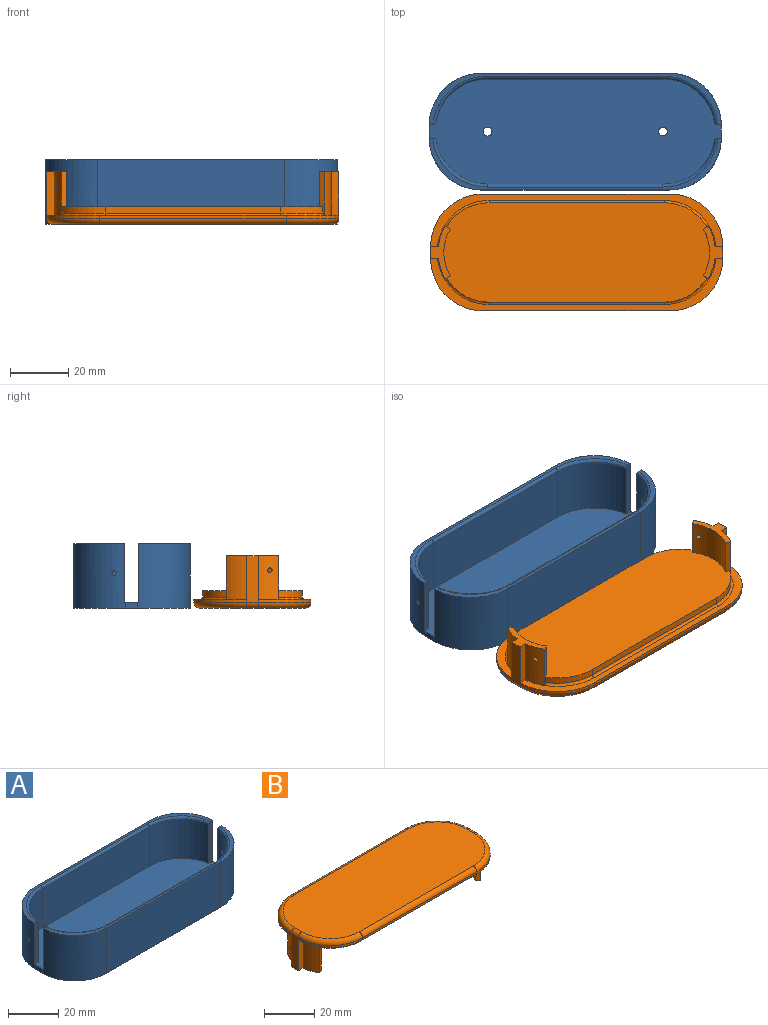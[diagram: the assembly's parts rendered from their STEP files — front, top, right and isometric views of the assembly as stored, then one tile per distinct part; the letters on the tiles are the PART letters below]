
ASSEMBLY  parts=2 mates=1
PART A: 32 faces, bbox 102.3x42.7x22 mm
  f0: plane 4x2mm, normal (1,0,0), area 8mm2, adj f3,f4,f13,f17
  f1: plane 99.99x17.5mm, normal (0,0,1), area 148.6mm2, adj f4,f5,f8,f11,f20,f21,f24,f27
  f2: cylinder r=18mm len=19mm, axis (0,0,-1), area 489.6mm2, adj f5,f14,f17,f27
  f3: cylinder r=18mm len=22mm, axis (0,0,1), area 610.2mm2, adj f0,f12,f13,f16,f17,f26,f29
  f4: cylinder r=18mm len=22mm, axis (0,0,-1), area 612mm2, adj f0,f1,f11,f13,f17,f27
  f5: torus R=19mm, axis (0,0,1), area 41.4mm2, adj f1,f2,f20,f27
  f6: plane 4x2mm, normal (-1,0,0), area 8mm2, adj f8,f9,f13,f17
  f7: cylinder r=18mm len=19mm, axis (0,0,1), area 489.6mm2, adj f10,f15,f17,f25
  f8: cylinder r=18mm len=22mm, axis (0,0,1), area 610.2mm2, adj f1,f6,f11,f13,f17,f24,f28
  f9: cylinder r=18mm len=22mm, axis (0,0,-1), area 612mm2, adj f6,f12,f13,f16,f17,f25
  f10: torus R=19mm, axis (0,0,1), area 41.4mm2, adj f7,f16,f23,f25
  f11: plane 64x22mm, normal (0,1,0), area 1408mm2, adj f1,f4,f8,f13
  f12: plane 64x22mm, normal (0,-1,0), area 1408mm2, adj f3,f9,f13,f16
  f13: plane 100x40mm, normal (0,0,-1), area 3707.7mm2, adj f0,f3,f4,f6,f8,f9,f11,f12
  f14: plane 60x19mm, normal (0,-1,0), area 1140mm2, adj f2,f17,f18,f20
  f15: plane 60x19mm, normal (0,1,0), area 1140mm2, adj f7,f17,f19,f23
  f16: plane 99.99x17.5mm, normal (0,0,1), area 148.6mm2, adj f3,f9,f10,f12,f22,f23,f25,f26
  f17: plane 100x36mm, normal (0,0,1), area 3184.3mm2, adj f0,f2,f3,f4,f6,f7,f8,f9
  f18: cylinder r=18mm len=19mm, axis (0,0,1), area 487.7mm2, adj f14,f17,f21,f24,f28
  f19: cylinder r=18mm len=19mm, axis (0,0,-1), area 487.7mm2, adj f15,f17,f22,f26,f29
  f20: cylinder r=1mm len=60mm, axis (-1,0,0), area 94.2mm2, adj f1,f5,f14,f21
  f21: torus R=19mm, axis (0,0,1), area 41.4mm2, adj f1,f18,f20,f24
  f22: torus R=19mm, axis (0,0,1), area 41.4mm2, adj f16,f19,f23,f26
  f23: cylinder r=1mm len=60mm, axis (1,0,0), area 94.2mm2, adj f10,f15,f16,f22
  f24: plane 20x2.17mm, normal (0,-1,0), area 43.1mm2, adj f1,f8,f17,f18,f21
  f25: plane 20x2.17mm, normal (0,1,0), area 43.1mm2, adj f7,f9,f10,f16,f17
  f26: plane 20x2.17mm, normal (0,1,0), area 43.1mm2, adj f3,f16,f17,f19,f22
  f27: plane 20x2.17mm, normal (0,-1,0), area 43.1mm2, adj f1,f2,f4,f5,f17
  f28: cylinder r=0.75mm len=3.02mm, axis (-1,0,0), area 12.2mm2, adj f8,f18
  f29: cylinder r=0.75mm len=3.02mm, axis (1,0,0), area 12.2mm2, adj f3,f19
  f30: cylinder r=1.5mm len=3mm, axis (0,0,1), area 18.8mm2, adj f13,f17
  f31: cylinder r=1.5mm len=3mm, axis (0,0,1), area 18.8mm2, adj f13,f17
PART B: 50 faces, bbox 103x43x18 mm
  f0: plane 15x2.62mm, normal (0,1,0), area 39.2mm2, adj f20,f23,f25,f42,f47
  f1: plane 15x2.62mm, normal (0,-1,0), area 39.2mm2, adj f3,f4,f20,f42,f46
  f2: cylinder r=17mm len=14.56mm, axis (0,0,1), area 38.5mm2, adj f4,f8,f13,f43
  f3: plane 100x18mm, normal (0,0,-1), area 286.3mm2, adj f1,f4,f6,f17,f18,f19,f24,f35
  f4: torus R=17.8mm, axis (0,0,1), area 24.7mm2, adj f1,f2,f3,f24,f43,f46
  f5: cylinder r=17mm len=14.56mm, axis (0,0,1), area 38.5mm2, adj f8,f9,f12,f39
  f6: torus R=17.8mm, axis (0,0,1), area 24.7mm2, adj f3,f7,f24,f35,f38,f40
  f7: cylinder r=17mm len=14.56mm, axis (0,0,1), area 38.5mm2, adj f6,f8,f13,f38
  f8: plane 91x34mm, normal (0,0,-1), area 2895mm2, adj f2,f5,f7,f11,f12,f13,f37,f38
  f9: torus R=17.8mm, axis (0,0,1), area 24.7mm2, adj f5,f10,f23,f26,f39,f41
  f10: plane 15x2.62mm, normal (0,1,0), area 39.2mm2, adj f9,f16,f23,f36,f41
  f11: cylinder r=17mm len=14.56mm, axis (0,0,1), area 38.5mm2, adj f8,f12,f25,f45
  f12: plane 60x2.2mm, normal (0,1,0), area 132mm2, adj f5,f8,f11,f26
  f13: plane 60x2.2mm, normal (0,-1,0), area 132mm2, adj f2,f7,f8,f24
  f14: plane 64x1mm, normal (0,1,0), area 64mm2, adj f15,f21,f23,f34
  f15: cylinder r=18mm len=18mm, axis (0,0,-1), area 28.3mm2, adj f14,f16,f23,f32
  f16: plane 16x4mm, normal (-1,0,0), area 64mm2, adj f10,f15,f17,f30,f35,f36
  f17: cylinder r=18mm len=18mm, axis (0,0,-1), area 28.3mm2, adj f3,f16,f18,f28
  f18: plane 64x1mm, normal (0,-1,0), area 64mm2, adj f3,f17,f19,f27
  f19: cylinder r=18mm len=18mm, axis (0,0,-1), area 28.3mm2, adj f3,f18,f20,f29
  f20: plane 16x4mm, normal (1,0,0), area 64mm2, adj f0,f1,f19,f21,f31,f42
  f21: cylinder r=18mm len=18mm, axis (0,0,-1), area 28.3mm2, adj f14,f20,f23,f33
  f22: plane 96x36mm, normal (0,0,1), area 3236.2mm2, adj f27,f28,f29,f30,f31,f32,f33,f34
  f23: plane 100x18mm, normal (0,0,-1), area 286.3mm2, adj f0,f9,f10,f14,f15,f21,f25,f26
  f24: cylinder r=0.8mm len=60mm, axis (1,0,0), area 75.4mm2, adj f3,f4,f6,f13
  f25: torus R=17.8mm, axis (0,0,1), area 24.7mm2, adj f0,f11,f23,f26,f45,f47
  f26: cylinder r=0.8mm len=60mm, axis (-1,0,0), area 75.4mm2, adj f9,f12,f23,f25
  f27: cylinder r=2mm len=64mm, axis (-1,0,0), area 201.1mm2, adj f18,f22,f28,f29
  f28: torus R=16mm, axis (0,0,1), area 85.2mm2, adj f17,f22,f27,f30
  f29: torus R=16mm, axis (0,0,1), area 85.2mm2, adj f19,f22,f27,f31
  f30: cylinder r=2mm len=4mm, axis (0,1,0), area 12.6mm2, adj f16,f22,f28,f32
  f31: cylinder r=2mm len=4mm, axis (0,-1,0), area 12.6mm2, adj f20,f22,f29,f33
  f32: torus R=16mm, axis (0,0,1), area 85.2mm2, adj f15,f22,f30,f34
  f33: torus R=16mm, axis (0,0,1), area 85.2mm2, adj f21,f22,f31,f34
  f34: cylinder r=2mm len=64mm, axis (1,0,0), area 201.1mm2, adj f14,f22,f32,f33
  f35: plane 15x2.62mm, normal (0,-1,0), area 39.2mm2, adj f3,f6,f16,f36,f40
  f36: plane 18.06x6.72mm, normal (0,0,-1), area 45.9mm2, adj f10,f16,f35,f37,f38,f39,f40,f41
  f37: cylinder r=15.5mm len=16mm, axis (0,0,-1), area 199.8mm2, adj f8,f36,f38,f39,f48
  f38: plane 14.94x1.71mm, normal (0.52,-0.86,0), area 25.4mm2, adj f6,f7,f8,f36,f37,f40
  f39: plane 14.94x1.71mm, normal (0.52,0.86,0), area 25.4mm2, adj f5,f8,f9,f36,f37,f41
  f40: cylinder r=17.5mm len=14.94mm, axis (0,0,-1), area 111.9mm2, adj f6,f35,f36,f38
  f41: cylinder r=17.5mm len=14.94mm, axis (0,0,-1), area 110mm2, adj f9,f10,f36,f39,f48
  f42: plane 18.06x6.72mm, normal (0,0,-1), area 45.9mm2, adj f0,f1,f20,f43,f44,f45,f46,f47
  f43: plane 14.94x1.71mm, normal (-0.52,-0.86,0), area 25.4mm2, adj f2,f4,f8,f42,f44,f46
  f44: cylinder r=15.5mm len=16mm, axis (0,0,-1), area 199.8mm2, adj f8,f42,f43,f45,f49
  f45: plane 14.94x1.71mm, normal (-0.52,0.86,0), area 25.4mm2, adj f8,f11,f25,f42,f44,f47
  f46: cylinder r=17.5mm len=14.94mm, axis (0,0,-1), area 110mm2, adj f1,f4,f42,f43,f49
  f47: cylinder r=17.5mm len=14.94mm, axis (0,0,-1), area 111.9mm2, adj f0,f25,f42,f45
  f48: cylinder r=0.75mm len=2.74mm, axis (-1,0,0), area 10.1mm2, adj f37,f41
  f49: cylinder r=0.75mm len=2.74mm, axis (1,0,0), area 10.1mm2, adj f44,f46
PLACE A t=(-20.38,0.32,-18.68)mm
PLACE B rot(axis=(1,0,0),180deg) t=(-19.88,-41.04,6.32)mm
MATE planar B.f22 <-> A.f13  axis (0,0,-1) through (-19.88,-41.04,-18.68)mm
